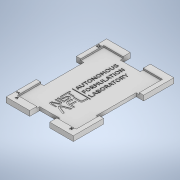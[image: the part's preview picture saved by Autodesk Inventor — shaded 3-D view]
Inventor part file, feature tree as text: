
AUTODESK INVENTOR PART (.ipt)
format: ipt  version: 2020 (Build 240168000, 168)  size: 1,314,304 bytes
history: native  units: in
note: dims shown in document units (in); Inventor stores cm internally (conversion verified against a paired STEP export)
features: sketch x5, extrude x4, emboss x1
ambient origin geometry x8: Origin, YZ Plane, XZ Plane, XY Plane, X Axis, Y Axis, Z Axis, Center Point
bodies: Solid1 (feature_tree)
feature tree (10):
  extrude  "Extrusion1"  Depth=5.0299in
  extrude  "Extrusion2"  TaperAngle=135.0deg  [1 undecoded]
  extrude  "Extrusion3"  Depth=1.0in
  extrude  "Extrusion4"  Depth=1.0in
  emboss  "Emboss1"
  sketch  "Sketch1"  dims[d0=3.3654in d1=5.0299in]
  sketch  "Sketch3"  dims[d2=1.0in d3=135.0deg]
  sketch  "Sketch4"  dims[d4=1.0in d5=1.0in]
  sketch  "Sketch5"  dims[d6=135.0deg d7=1.0in]
  sketch  "Sketch6"  dims[d8=45.0deg d9=0.25in d10=0.0in d26=2.9291in d27=4.315in d28=0.0787in d29=0.0in d30=0.5in d31=2.0in d32=1.0in d33=0.5in d34=0.5in d35=2.0in d36=1.0in d37=0.5in d38=0.5in d39=0.0in d40=0.5in d41=0.375in d42=2.0in d43=0.375in d44=0.0197in d45=0.0in d46=0.0197in d47=0.0in]
note: 1 required parameter value undecoded (feature->parameter linkage not recoverable at this tier; creation-order binding heuristic only, values carry confidence <= 0.55)
